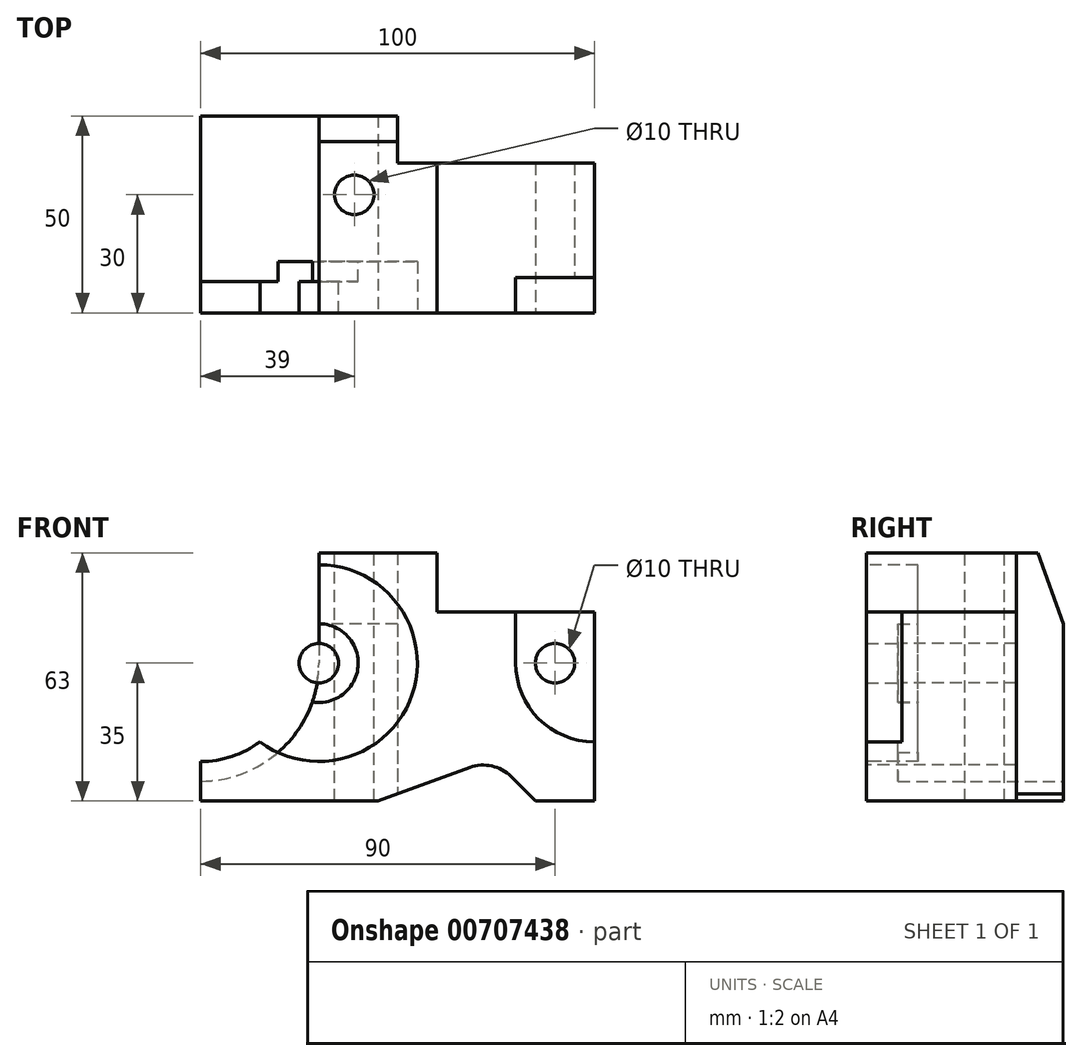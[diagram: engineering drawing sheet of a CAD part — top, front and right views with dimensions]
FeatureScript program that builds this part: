
annotation { "Feature Type Name" : "Feature", "Feature Type Description" : "" }
export const myFeature = defineFeature(function(context is Context, id is Id, definition is map)
    precondition{}
    {
        {
            var Q0;
            Q0=qCreatedBy(makeId("Front.planeOp"),FACE);
            var sketch = newSketch(context, id + "F0", { "sketchPlane" : qUnion([Q0])});
            skLineSegment(sketch, "E0.bottom", {"start": v(50, -31.5) * mm, "end": v(-50, -31.5) * mm});
            skLineSegment(sketch, "E0.top", {"start": v(50, 31.5) * mm, "end": v(-50, 31.5) * mm});
            skLineSegment(sketch, "E0.left", {"start": v(50, -31.5) * mm, "end": v(50, 31.5) * mm});
            skLineSegment(sketch, "E0.right", {"start": v(-50, -31.5) * mm, "end": v(-50, 31.5) * mm});
            skPoint(sketch, "E0.middle", {"position": v(0, 0) * mm});
            skSolve(sketch);
        }
        {
            var Q0;
            Q0 = qSketchRegion(id + "F0", true);
            extrude(context, id + "F1", {"entities" : qUnion([Q0]), "depth" : 50 * mm, "offsetDistance" : 25 * mm});
        }
        {
            var Q0;
            Q0=makeQuery(id+"F1.opExtrude","CAP_FACE",FACE,{"disambiguationData":[OSD([sQuery(id+"F0.wireOp",EDGE,"E0.bottom"),sQuery(id+"F0.wireOp",EDGE,"E0.top"),sQuery(id+"F0.wireOp",EDGE,"E0.left"),sQuery(id+"F0.wireOp",EDGE,"E0.right")])],"isStart":false});
            var sketch = newSketch(context, id + "F2", { "sketchPlane" : qUnion([Q0])});
            skLineSegment(sketch, "E1.bottom", {"start": v(10, 31.5) * mm, "end": v(50, 31.5) * mm});
            skLineSegment(sketch, "E1.top", {"start": v(10, 16.5) * mm, "end": v(50, 16.5) * mm});
            skLineSegment(sketch, "E1.left", {"start": v(10, 31.5) * mm, "end": v(10, 16.5) * mm});
            skLineSegment(sketch, "E1.right", {"start": v(50, 31.5) * mm, "end": v(50, 16.5) * mm});
            skSolve(sketch);
        }
        {
            var Q0;
            Q0 = qSketchRegion(id + "F2", true);
            extrude(context, id + "F3", {"entities" : qUnion([Q0]), "operationType" : NewBodyOperationType.REMOVE, "endBound" : BoundingType.THROUGH_ALL, "oppositeDirection" : true, "depth" : 25 * mm, "offsetDistance" : 25 * mm});
        }
        {
            var Q0;
            Q0=makeQuery(id+"F1.opExtrude","CAP_FACE",FACE,{"disambiguationData":[OSD([sQuery(id+"F0.wireOp",EDGE,"E0.bottom"),sQuery(id+"F0.wireOp",EDGE,"E0.top"),sQuery(id+"F0.wireOp",EDGE,"E0.left"),sQuery(id+"F0.wireOp",EDGE,"E0.right")])],"isStart":false});
            var sketch = newSketch(context, id + "F4", { "sketchPlane" : qUnion([Q0])});
            skArc(sketch, "E2", {"start": v(30, 3.5) * mm, "mid": v(35.86, -10.64) * mm, "end": v(50, -16.5) * mm});
            skPoint(sketch, "E3", {"position": v(50, -7.5) * mm});
            skLineSegment(sketch, "E4", {"start": v(30, 16.5) * mm, "end": v(30, 3.5) * mm});
            skLineSegment(sketch, "E5", {"start": v(30, 16.5) * mm, "end": v(50, 16.5) * mm});
            skLineSegment(sketch, "E6", {"start": v(50, 16.5) * mm, "end": v(50, -16.5) * mm});
            skSolve(sketch);
        }
        {
            var Q0;
            Q0 = qSketchRegion(id + "F4", true);
            extrude(context, id + "F5", {"entities" : qUnion([Q0]), "operationType" : NewBodyOperationType.REMOVE, "oppositeDirection" : true, "depth" : 9 * mm, "offsetDistance" : 25 * mm});
        }
        {
            var Q0;
            Q0=makeQuery(id+"F5.boolean.opBoolean","COPY",FACE,{"derivedFrom":makeQuery(id+"F5.opExtrude","CAP_FACE",FACE,{"disambiguationData":[OSD([sQuery(id+"F4.wireOp",EDGE,"E2"),sQuery(id+"F4.wireOp",EDGE,"E4"),sQuery(id+"F4.wireOp",EDGE,"E5"),sQuery(id+"F4.wireOp",EDGE,"E6")])],"isStart":false})});
            var sketch = newSketch(context, id + "F6", { "sketchPlane" : qUnion([Q0])});
            skCircle(sketch, "E7", {"center": v(40, 3.5) * mm, "radius": 5 * mm});
            skSolve(sketch);
        }
        {
            var Q0;
            Q0 = qSketchRegion(id + "F6", true);
            extrude(context, id + "F7", {"entities" : qUnion([Q0]), "operationType" : NewBodyOperationType.REMOVE, "endBound" : BoundingType.THROUGH_ALL, "oppositeDirection" : true, "depth" : 25 * mm, "offsetDistance" : 25 * mm});
        }
        {
            var Q0;
            Q0=makeQuery(id+"F1.opExtrude","CAP_FACE",FACE,{"disambiguationData":[OSD([sQuery(id+"F0.wireOp",EDGE,"E0.bottom"),sQuery(id+"F0.wireOp",EDGE,"E0.top"),sQuery(id+"F0.wireOp",EDGE,"E0.left"),sQuery(id+"F0.wireOp",EDGE,"E0.right")])],"isStart":true});
            var sketch = newSketch(context, id + "F8", { "sketchPlane" : qUnion([Q0])});
            skLineSegment(sketch, "E8.bottom", {"start": v(0, 31.5) * mm, "end": v(-50, 31.5) * mm});
            skLineSegment(sketch, "E8.top", {"start": v(0, -31.5) * mm, "end": v(-50, -31.5) * mm});
            skLineSegment(sketch, "E8.left", {"start": v(0, 31.5) * mm, "end": v(0, -31.5) * mm});
            skLineSegment(sketch, "E8.right", {"start": v(-50, 31.5) * mm, "end": v(-50, -31.5) * mm});
            skSolve(sketch);
        }
        {
            var Q0;
            Q0 = qSketchRegion(id + "F8", true);
            extrude(context, id + "F9", {"entities" : qUnion([Q0]), "operationType" : NewBodyOperationType.REMOVE, "oppositeDirection" : true, "depth" : 12 * mm, "offsetDistance" : 25 * mm});
        }
        {
            var Q0;
            Q0=makeQuery(id+"F1.opExtrude","CAP_FACE",FACE,{"disambiguationData":[OSD([sQuery(id+"F0.wireOp",EDGE,"E0.bottom"),sQuery(id+"F0.wireOp",EDGE,"E0.top"),sQuery(id+"F0.wireOp",EDGE,"E0.left"),sQuery(id+"F0.wireOp",EDGE,"E0.right")])],"isStart":false});
            var sketch = newSketch(context, id + "F10", { "sketchPlane" : qUnion([Q0])});
            skLineSegment(sketch, "E9", {"start": v(35, -31.5) * mm, "end": v(28.83, -25.33) * mm});
            skLineSegment(sketch, "E10", {"start": v(-5, -31.5) * mm, "end": v(18.34, -23) * mm});
            skArc(sketch, "E11", {"start": v(28.83, -25.33) * mm, "mid": v(23.92, -22.64) * mm, "end": v(18.34, -23) * mm});
            skLineSegment(sketch, "E12", {"start": v(-5, -31.5) * mm, "end": v(35, -31.5) * mm});
            skSolve(sketch);
        }
        {
            var Q0;
            Q0 = qSketchRegion(id + "F10", true);
            extrude(context, id + "F11", {"entities" : qUnion([Q0]), "operationType" : NewBodyOperationType.REMOVE, "endBound" : BoundingType.THROUGH_ALL, "oppositeDirection" : true, "depth" : 25 * mm, "offsetDistance" : 25 * mm});
        }
        {
            var Q0;
            Q0=makeQuery(id+"F1.opExtrude","CAP_FACE",FACE,{"disambiguationData":[OSD([sQuery(id+"F0.wireOp",EDGE,"E0.bottom"),sQuery(id+"F0.wireOp",EDGE,"E0.top"),sQuery(id+"F0.wireOp",EDGE,"E0.left"),sQuery(id+"F0.wireOp",EDGE,"E0.right")])],"isStart":false});
            var sketch = newSketch(context, id + "F12", { "sketchPlane" : qUnion([Q0])});
            skCircle(sketch, "E13", {"center": v(-20, 3.5) * mm, "radius": 25 * mm});
            skSolve(sketch);
        }
        {
            var Q0;
            Q0 = qSketchRegion(id + "F12", true);
            extrude(context, id + "F13", {"entities" : qUnion([Q0]), "operationType" : NewBodyOperationType.REMOVE, "oppositeDirection" : true, "depth" : 13 * mm, "offsetDistance" : 25 * mm});
        }
        {
            var Q0;
            Q0=makeQuery(id+"F13.boolean.opBoolean","COPY",FACE,{"derivedFrom":makeQuery(id+"F13.opExtrude","CAP_FACE",FACE,{"disambiguationData":[OSD([sQuery(id+"F12.wireOp",EDGE,"E13")])],"isStart":false})});
            var sketch = newSketch(context, id + "F14", { "sketchPlane" : qUnion([Q0])});
            skCircle(sketch, "E14", {"center": v(-20, 3.5) * mm, "radius": 10 * mm});
            skSolve(sketch);
        }
        {
            var Q0;
            Q0 = qSketchRegion(id + "F14", true);
            extrude(context, id + "F15", {"entities" : qUnion([Q0]), "operationType" : NewBodyOperationType.ADD, "depth" : (13 - 8) * mm, "offsetDistance" : 25 * mm});
        }
        {
            var Q0;
            Q0=makeQuery(id+"F15.opExtrude","CAP_FACE",FACE,{"disambiguationData":[OSD([sQuery(id+"F14.wireOp",EDGE,"E14")])],"isStart":false});
            var sketch = newSketch(context, id + "F16", { "sketchPlane" : qUnion([Q0])});
            skCircle(sketch, "E15", {"center": v(-20, 3.5) * mm, "radius": 5 * mm});
            skSolve(sketch);
        }
        {
            var Q0;
            Q0 = qSketchRegion(id + "F16", true);
            extrude(context, id + "F17", {"entities" : qUnion([Q0]), "operationType" : NewBodyOperationType.ADD, "depth" : 8 * mm, "offsetDistance" : 25 * mm});
        }
        {
            var Q0;
            Q0=makeQuery(id+"F1.opExtrude","CAP_FACE",FACE,{"disambiguationData":[OSD([sQuery(id+"F0.wireOp",EDGE,"E0.bottom"),sQuery(id+"F0.wireOp",EDGE,"E0.top"),sQuery(id+"F0.wireOp",EDGE,"E0.left"),sQuery(id+"F0.wireOp",EDGE,"E0.right")])],"isStart":true});
            var sketch = newSketch(context, id + "F18", { "sketchPlane" : qUnion([Q0])});
            skArc(sketch, "E16", {"start": v(20, 3.5) * mm, "mid": v(28.79, -17.71) * mm, "end": v(50, -26.5) * mm});
            skLineSegment(sketch, "E17", {"start": v(20, 31.5) * mm, "end": v(20, 3.5) * mm});
            skLineSegment(sketch, "E18", {"start": v(20, 31.5) * mm, "end": v(50, 31.5) * mm});
            skLineSegment(sketch, "E19", {"start": v(50, 31.5) * mm, "end": v(50, -26.5) * mm});
            skSolve(sketch);
        }
        {
            var Q0;
            Q0 = qSketchRegion(id + "F18", true);
            extrude(context, id + "F19", {"entities" : qUnion([Q0]), "operationType" : NewBodyOperationType.REMOVE, "oppositeDirection" : true, "depth" : (50 - 8) * mm, "offsetDistance" : 25 * mm});
        }
        {
            var Q0;
            Q0=makeQuery(id+"F1.opExtrude","CAP_FACE",FACE,{"disambiguationData":[OSD([sQuery(id+"F0.wireOp",EDGE,"E0.bottom"),sQuery(id+"F0.wireOp",EDGE,"E0.top"),sQuery(id+"F0.wireOp",EDGE,"E0.left"),sQuery(id+"F0.wireOp",EDGE,"E0.right")])],"isStart":false});
            var sketch = newSketch(context, id + "F20", { "sketchPlane" : qUnion([Q0])});
            skArc(sketch, "E20", {"start": v(-50, -21.5) * mm, "mid": v(-32.32, -14.18) * mm, "end": v(-25, 3.5) * mm});
            skLineSegment(sketch, "E21", {"start": v(-25, 26.2) * mm, "end": v(-25, 3.5) * mm});
            skLineSegment(sketch, "E22", {"start": v(-25, 31.5) * mm, "end": v(-50, 31.5) * mm});
            skLineSegment(sketch, "E23", {"start": v(-50, 31.5) * mm, "end": v(-50, -21.5) * mm});
            skLineSegment(sketch, "E24", {"start": v(-25, 31.5) * mm, "end": v(-20, 31.5) * mm});
            skLineSegment(sketch, "E25", {"start": v(-20, 31.5) * mm, "end": v(-20, 26.2) * mm});
            skLineSegment(sketch, "E26", {"start": v(-20, 26.2) * mm, "end": v(-25, 26.2) * mm});
            skSolve(sketch);
        }
        {
            var Q0;
            Q0 = qSketchRegion(id + "F20", true);
            extrude(context, id + "F21", {"entities" : qUnion([Q0]), "operationType" : NewBodyOperationType.REMOVE, "oppositeDirection" : true, "depth" : 8 * mm, "offsetDistance" : 25 * mm});
        }
        {
            var Q0;
            Q0=makeQuery(id+"F21.boolean.opBoolean","MERGE",FACE,{"derivedFrom":[makeQuery(id+"F19.boolean.opBoolean","COPY",FACE,{"derivedFrom":makeQuery(id+"F19.opExtrude","SWEPT_FACE",FACE,{"disambiguationData":[OSD([sQuery(id+"F18.wireOp",EDGE,"E17")])]})}),makeQuery(id+"F21.opExtrude","SWEPT_FACE",FACE,{"disambiguationData":[OSD([sQuery(id+"F20.wireOp",EDGE,"E25")])]})]});
            var sketch = newSketch(context, id + "F22", { "sketchPlane" : qUnion([Q0])});
            skLineSegment(sketch, "E27", {"start": v(0, 31.5) * mm, "end": v(6.55, 31.5) * mm});
            skLineSegment(sketch, "E28", {"start": v(0, 31.5) * mm, "end": v(0, 13.5) * mm});
            skLineSegment(sketch, "E29", {"start": v(0, 13.5) * mm, "end": v(6.55, 31.5) * mm});
            skSolve(sketch);
        }
        {
            var Q0;
            Q0 = qSketchRegion(id + "F22", true);
            extrude(context, id + "F23", {"entities" : qUnion([Q0]), "operationType" : NewBodyOperationType.REMOVE, "endBound" : BoundingType.THROUGH_ALL, "oppositeDirection" : true, "depth" : 25 * mm, "offsetDistance" : 25 * mm});
        }
        {
            var Q0;
            Q0=makeQuery(id+"F1.opExtrude","SWEPT_FACE",FACE,{"disambiguationData":[OSD([sQuery(id+"F0.wireOp",EDGE,"E0.top")])]});
            var sketch = newSketch(context, id + "F24", { "sketchPlane" : qUnion([Q0])});
            skCircle(sketch, "E30", {"center": v(-11, -20) * mm, "radius": 5 * mm});
            skSolve(sketch);
        }
        {
            var Q0;
            Q0 = qSketchRegion(id + "F24", true);
            extrude(context, id + "F25", {"entities" : qUnion([Q0]), "operationType" : NewBodyOperationType.REMOVE, "endBound" : BoundingType.THROUGH_ALL, "oppositeDirection" : true, "depth" : 25 * mm, "offsetDistance" : 25 * mm});
        }
    });
